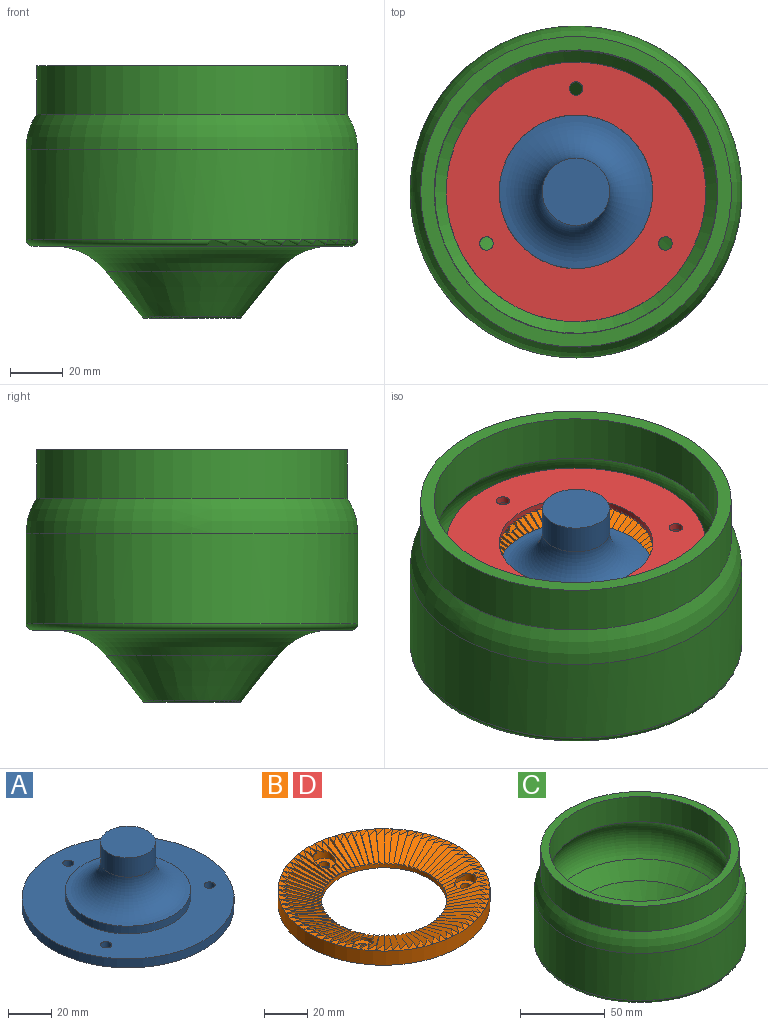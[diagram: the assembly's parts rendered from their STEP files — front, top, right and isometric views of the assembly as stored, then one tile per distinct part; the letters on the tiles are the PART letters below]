
ASSEMBLY  parts=4 mates=3
PART A: 10 faces, bbox 98x98x36.7 mm
  f0: cylinder r=12.7mm len=25.4mm, axis (0,0,1), area 874.5mm2, adj f1,f6
  f1: torus R=28.95mm, axis (0,0,1), area 2983.7mm2, adj f0,f2
  f2: cylinder r=28.95mm len=57.9mm, axis (0,0,1), area 794.3mm2, adj f1,f3
  f3: plane 98x98mm, normal (0,0,1), area 4848.7mm2, adj f2,f4,f7,f8,f9
  f4: cylinder r=49mm len=98mm, axis (0,0,1), area 1564mm2, adj f3,f5
  f5: plane 98x98mm, normal (0,0,-1), area 7481.5mm2, adj f4,f7,f8,f9
  f6: plane 25.4x25.4mm, normal (0,0,1), area 506.7mm2, adj f0
  f7: cylinder r=2.55mm len=5.11mm, axis (0,0,1), area 81.5mm2, adj f3,f5
  f8: cylinder r=2.55mm len=5.11mm, axis (0,0,1), area 81.5mm2, adj f3,f5
  f9: cylinder r=2.55mm len=5.11mm, axis (0,0,1), area 81.5mm2, adj f3,f5
PART B: 188 faces, bbox 98x98x8 mm
  f0: plane 5.82x2.75mm, normal (0.35,-0.3,0.89), area 14.5mm2, adj f18,f20,f24,f179
  f1: plane 4.04x2.48mm, normal (0.52,0.85,0), area 3.4mm2, adj f25,f74,f93,f183
  f2: plane 4.27x2.62mm, normal (0.52,0.85,0), area 5mm2, adj f3,f8,f24,f183
  f3: plane 5.84x4.62mm, normal (-0.42,-0.17,0.89), area 13.9mm2, adj f2,f5,f24,f183
  f4: plane 4.55x2.32mm, normal (0.45,0.89,0), area 3.9mm2, adj f25,f74,f75,f183
  f5: plane 4.72x2.67mm, normal (0.45,0.89,0), area 5.3mm2, adj f3,f24,f75,f183
  f6: plane 5.57x4.05mm, normal (0.59,0.81,0), area 6.3mm2, adj f25,f90,f93,f183
  f7: plane 5.47x3.97mm, normal (0.59,0.81,0), area 6.9mm2, adj f8,f24,f90,f183
  f8: plane 5.88x5.55mm, normal (-0.43,-0.14,0.89), area 15.8mm2, adj f2,f7,f24,f183
  f9: plane 5.84x4.62mm, normal (0.07,0.45,0.89), area 13.9mm2, adj f11,f16,f24,f181
  f10: plane 4.55x2.32mm, normal (0.45,-0.89,0), area 3.9mm2, adj f25,f137,f139,f181
  f11: plane 4.72x2.67mm, normal (0.45,-0.89,0), area 5.3mm2, adj f9,f24,f139,f181
  f12: plane 5.88x5.55mm, normal (0.04,0.45,0.89), area 15.8mm2, adj f14,f16,f24,f181
  f13: plane 5.57x4.05mm, normal (0.59,-0.81,0), area 6.3mm2, adj f25,f143,f144,f181
  f14: plane 5.47x3.97mm, normal (0.59,-0.81,0), area 6.9mm2, adj f12,f24,f144,f181
  f15: plane 4.04x2.48mm, normal (0.52,-0.85,0), area 3.4mm2, adj f25,f137,f143,f181
  f16: plane 4.27x2.62mm, normal (0.52,-0.85,0), area 5mm2, adj f9,f12,f24,f181
  f17: plane 5.75x1.73mm, normal (-1,0.08,0), area 4.8mm2, adj f25,f33,f150,f179
  f18: plane 5.81x2.84mm, normal (-1,0.08,0), area 5.8mm2, adj f0,f24,f150,f179
  f19: plane 4.63x1.39mm, normal (-1,0,0), area 3.2mm2, adj f25,f33,f167,f179
  f20: plane 4.92x2.54mm, normal (-1,0,0), area 4.9mm2, adj f0,f21,f24,f179
  f21: plane 5.82x2.86mm, normal (0.37,-0.27,0.89), area 14.5mm2, adj f20,f23,f24,f179
  f22: plane 5.75x1.73mm, normal (-1,-0.08,0), area 4.8mm2, adj f25,f167,f168,f179
  f23: plane 5.81x2.84mm, normal (-1,-0.08,0), area 5.8mm2, adj f21,f24,f168,f179
  f24: cylinder r=29mm len=58mm, axis (0,0,1), area 463.4mm2, adj f0,f2,f3,f5,f7,f8,f9,f11
  f25: plane 98x98mm, normal (0,0,1), area 803.3mm2, adj f1,f4,f6,f10,f13,f15,f17,f19
  f26: cylinder r=49mm len=98mm, axis (0,0,1), area 2463mm2, adj f25,f27
  f27: plane 98x98mm, normal (0,0,-1), area 4839.5mm2, adj f24,f26,f185,f186,f187
  f28: plane 19.16x5.91mm, normal (-0.97,0.23,0), area 20.5mm2, adj f24,f25,f29,f31
  f29: plane 19.18x6.85mm, normal (0.29,-0.35,0.89), area 57.5mm2, adj f24,f25,f28,f30
  f30: plane 19.46x5.91mm, normal (-0.99,0.16,0), area 20.5mm2, adj f24,f25,f29,f150
  f31: plane 18.76x8.3mm, normal (0.27,-0.37,0.89), area 57.5mm2, adj f24,f25,f28,f40
  f32: plane 18.21x7.54mm, normal (-0.38,-0.92,0), area 20.5mm2, adj f24,f25,f130,f151
  f33: plane 5.75x3.82mm, normal (0.35,-0.3,0.89), area 10.3mm2, adj f17,f19,f25,f179
  f34: plane 18.21x7.54mm, normal (0.92,0.38,0), area 20.5mm2, adj f24,f25,f86,f94
  f35: plane 19.65x5.91mm, normal (-0.08,1,0), area 20.5mm2, adj f24,f25,f57,f66
  f36: plane 14.99x12.8mm, normal (-0.65,0.76,0), area 20.5mm2, adj f24,f25,f48,f65
  f37: plane 17.56x8.95mm, normal (-0.89,0.45,0), area 20.5mm2, adj f24,f25,f41,f45
  f38: plane 18.21x7.54mm, normal (-0.92,0.38,0), area 20.5mm2, adj f24,f25,f39,f41
  f39: plane 18.22x9.69mm, normal (0.24,-0.39,0.89), area 57.5mm2, adj f24,f25,f38,f40
  f40: plane 18.74x6.09mm, normal (-0.95,0.31,0), area 20.5mm2, adj f24,f25,f31,f39
  f41: plane 17.57x11.03mm, normal (0.21,-0.4,0.89), area 57.5mm2, adj f24,f25,f37,f38
  f42: plane 15.96x13.49mm, normal (0.14,-0.43,0.89), area 57.5mm2, adj f24,f25,f43,f44
  f43: plane 15.94x11.58mm, normal (-0.81,0.59,0), area 20.5mm2, adj f24,f25,f42,f46
  f44: plane 16.8x10.3mm, normal (-0.85,0.52,0), area 20.5mm2, adj f24,f25,f42,f45
  f45: plane 16.82x12.3mm, normal (0.17,-0.42,0.89), area 57.5mm2, adj f24,f25,f37,f44
  f46: plane 15x14.6mm, normal (0.11,-0.44,0.89), area 57.5mm2, adj f24,f25,f43,f47
  f47: plane 14.99x12.8mm, normal (-0.76,0.65,0), area 20.5mm2, adj f24,f25,f46,f50
  f48: plane 16.54x12.81mm, normal (0.04,-0.45,0.89), area 57.5mm2, adj f24,f25,f36,f49
  f49: plane 13.93x13.93mm, normal (-0.71,0.71,0), area 20.5mm2, adj f24,f25,f48,f50
  f50: plane 15.62x13.95mm, normal (0.07,-0.45,0.89), area 57.5mm2, adj f24,f25,f47,f49
  f51: plane 19.54x7.93mm, normal (-0.14,-0.43,0.89), area 57.5mm2, adj f24,f25,f53,f64
  f52: plane 19.16x5.91mm, normal (-0.23,0.97,0), area 20.5mm2, adj f24,f25,f54,f56
  f53: plane 18.74x6.09mm, normal (-0.31,0.95,0), area 20.5mm2, adj f24,f25,f51,f54
  f54: plane 19.79x6.87mm, normal (-0.17,-0.42,0.89), area 57.5mm2, adj f24,f25,f52,f53
  f55: plane 19.46x5.91mm, normal (-0.16,0.99,0), area 20.5mm2, adj f24,f25,f56,f57
  f56: plane 19.92x5.93mm, normal (-0.21,-0.4,0.89), area 57.5mm2, adj f24,f25,f52,f55
  f57: plane 19.93x5.93mm, normal (-0.24,-0.39,0.89), area 57.5mm2, adj f24,f25,f35,f55
  f58: plane 19.17x8.93mm, normal (-0.11,-0.44,0.89), area 57.5mm2, adj f24,f25,f60,f64
  f59: plane 18.69x9.89mm, normal (-0.07,-0.45,0.89), area 57.5mm2, adj f24,f25,f60,f63
  f60: plane 17.56x8.95mm, normal (-0.45,0.89,0), area 20.5mm2, adj f24,f25,f58,f59
  f61: plane 18.08x10.78mm, normal (-0.04,-0.45,0.89), area 57.5mm2, adj f24,f25,f62,f63
  f62: plane 15.94x11.58mm, normal (-0.59,0.81,0), area 20.5mm2, adj f24,f25,f61,f65
  f63: plane 16.8x10.3mm, normal (-0.52,0.85,0), area 20.5mm2, adj f24,f25,f59,f61
  f64: plane 18.21x7.54mm, normal (-0.38,0.92,0), area 20.5mm2, adj f24,f25,f51,f58
  f65: plane 17.37x11.6mm, normal (0,-0.45,0.89), area 57.5mm2, adj f24,f25,f36,f62
  f66: plane 19.81x5.93mm, normal (-0.27,-0.37,0.89), area 57.5mm2, adj f24,f25,f35,f69
  f67: plane 19.16x5.91mm, normal (0.23,0.97,0), area 20.5mm2, adj f24,f25,f73,f79
  f68: plane 19.65x5.91mm, normal (0.08,1,0), area 20.5mm2, adj f24,f25,f70,f72
  f69: plane 19.71x5.91mm, normal (0,1,0), area 20.5mm2, adj f24,f25,f66,f70
  f70: plane 19.66x5.93mm, normal (-0.3,-0.35,0.89), area 57.5mm2, adj f24,f25,f68,f69
  f71: plane 19.46x5.91mm, normal (0.16,0.99,0), area 20.5mm2, adj f24,f25,f72,f73
  f72: plane 19.48x5.93mm, normal (-0.32,-0.32,0.89), area 57.5mm2, adj f24,f25,f68,f71
  f73: plane 19.18x6.85mm, normal (-0.35,-0.29,0.89), area 57.5mm2, adj f24,f25,f67,f71
  f74: plane 5.66x4.04mm, normal (-0.42,-0.17,0.89), area 9.4mm2, adj f1,f4,f25,f183
  f75: plane 17.57x11.03mm, normal (-0.4,-0.21,0.89), area 34.6mm2, adj f4,f5,f24,f25,f78,f183
  f76: plane 18.22x9.69mm, normal (-0.39,-0.24,0.89), area 57.5mm2, adj f24,f25,f77,f78
  f77: plane 18.74x6.09mm, normal (0.31,0.95,0), area 20.5mm2, adj f24,f25,f76,f79
  f78: plane 18.21x7.54mm, normal (0.38,0.92,0), area 20.5mm2, adj f24,f25,f75,f76
  f79: plane 18.76x8.3mm, normal (-0.37,-0.27,0.89), area 57.5mm2, adj f24,f25,f67,f77
  f80: plane 17.37x11.6mm, normal (-0.45,0,0.89), area 57.5mm2, adj f24,f25,f82,f92
  f81: plane 16.8x10.3mm, normal (0.85,0.52,0), area 20.5mm2, adj f24,f25,f83,f85
  f82: plane 15.94x11.58mm, normal (0.81,0.59,0), area 20.5mm2, adj f24,f25,f80,f83
  f83: plane 18.08x10.78mm, normal (-0.45,0.04,0.89), area 57.5mm2, adj f24,f25,f81,f82
  f84: plane 17.56x8.95mm, normal (0.89,0.45,0), area 20.5mm2, adj f24,f25,f85,f86
  f85: plane 18.69x9.89mm, normal (-0.45,0.07,0.89), area 57.5mm2, adj f24,f25,f81,f84
  f86: plane 19.17x8.93mm, normal (-0.44,0.11,0.89), area 57.5mm2, adj f24,f25,f34,f84
  f87: plane 16.54x12.81mm, normal (-0.45,-0.04,0.89), area 57.5mm2, adj f24,f25,f89,f92
  f88: plane 15.62x13.95mm, normal (-0.45,-0.07,0.89), area 57.5mm2, adj f24,f25,f89,f91
  f89: plane 13.93x13.93mm, normal (0.71,0.71,0), area 20.5mm2, adj f24,f25,f87,f88
  f90: plane 15x14.6mm, normal (-0.44,-0.11,0.89), area 52.8mm2, adj f6,f7,f24,f25,f91,f183
  f91: plane 14.99x12.8mm, normal (0.65,0.76,0), area 20.5mm2, adj f24,f25,f88,f90
  f92: plane 14.99x12.8mm, normal (0.76,0.65,0), area 20.5mm2, adj f24,f25,f80,f87
  f93: plane 5.66x5.57mm, normal (-0.43,-0.14,0.89), area 12.4mm2, adj f1,f6,f25,f183
  f94: plane 19.54x7.93mm, normal (-0.43,0.14,0.89), area 57.5mm2, adj f24,f25,f34,f99
  f95: plane 14.99x12.8mm, normal (0.76,-0.65,0), area 20.5mm2, adj f24,f25,f121,f149
  f96: plane 19.16x5.91mm, normal (0.97,-0.23,0), area 20.5mm2, adj f24,f25,f104,f111
  f97: plane 19.65x5.91mm, normal (1,0.08,0), area 20.5mm2, adj f24,f25,f103,f110
  f98: plane 19.16x5.91mm, normal (0.97,0.23,0), area 20.5mm2, adj f24,f25,f100,f102
  f99: plane 18.74x6.09mm, normal (0.95,0.31,0), area 20.5mm2, adj f24,f25,f94,f100
  f100: plane 19.79x6.87mm, normal (-0.42,0.17,0.89), area 57.5mm2, adj f24,f25,f98,f99
  f101: plane 19.46x5.91mm, normal (0.99,0.16,0), area 20.5mm2, adj f24,f25,f102,f103
  f102: plane 19.92x5.93mm, normal (-0.4,0.21,0.89), area 57.5mm2, adj f24,f25,f98,f101
  f103: plane 19.93x5.93mm, normal (-0.39,0.24,0.89), area 57.5mm2, adj f24,f25,f97,f101
  f104: plane 19.18x6.85mm, normal (-0.29,0.35,0.89), area 57.5mm2, adj f24,f25,f96,f106
  f105: plane 19.48x5.93mm, normal (-0.32,0.32,0.89), area 57.5mm2, adj f24,f25,f106,f109
  f106: plane 19.46x5.91mm, normal (0.99,-0.16,0), area 20.5mm2, adj f24,f25,f104,f105
  f107: plane 19.66x5.93mm, normal (-0.35,0.3,0.89), area 57.5mm2, adj f24,f25,f108,f109
  f108: plane 19.71x5.91mm, normal (1,0,0), area 20.5mm2, adj f24,f25,f107,f110
  f109: plane 19.65x5.91mm, normal (1,-0.08,0), area 20.5mm2, adj f24,f25,f105,f107
  f110: plane 19.81x5.93mm, normal (-0.37,0.27,0.89), area 57.5mm2, adj f24,f25,f97,f108
  f111: plane 18.76x8.3mm, normal (-0.27,0.37,0.89), area 57.5mm2, adj f24,f25,f96,f113
  f112: plane 18.21x7.54mm, normal (0.92,-0.38,0), area 20.5mm2, adj f24,f25,f114,f115
  f113: plane 18.74x6.09mm, normal (0.95,-0.31,0), area 20.5mm2, adj f24,f25,f111,f114
  f114: plane 18.22x9.69mm, normal (-0.24,0.39,0.89), area 57.5mm2, adj f24,f25,f112,f113
  f115: plane 17.57x11.03mm, normal (-0.21,0.4,0.89), area 57.5mm2, adj f24,f25,f112,f117
  f116: plane 16.8x10.3mm, normal (0.85,-0.52,0), area 20.5mm2, adj f24,f25,f118,f120
  f117: plane 17.56x8.95mm, normal (0.89,-0.45,0), area 20.5mm2, adj f24,f25,f115,f118
  f118: plane 16.82x12.3mm, normal (-0.17,0.42,0.89), area 57.5mm2, adj f24,f25,f116,f117
  f119: plane 15.94x11.58mm, normal (0.81,-0.59,0), area 20.5mm2, adj f24,f25,f120,f121
  f120: plane 15.96x13.49mm, normal (-0.14,0.43,0.89), area 57.5mm2, adj f24,f25,f116,f119
  f121: plane 15x14.6mm, normal (-0.11,0.44,0.89), area 57.5mm2, adj f24,f25,f95,f119
  f122: plane 19.92x5.93mm, normal (0.21,0.4,0.89), area 57.5mm2, adj f24,f25,f125,f148
  f123: plane 19.65x5.91mm, normal (-0.08,-1,0), area 20.5mm2, adj f24,f25,f129,f136
  f124: plane 19.65x5.91mm, normal (0.08,-1,0), area 20.5mm2, adj f24,f25,f126,f128
  f125: plane 19.46x5.91mm, normal (0.16,-0.99,0), area 20.5mm2, adj f24,f25,f122,f126
  f126: plane 19.93x5.93mm, normal (0.24,0.39,0.89), area 57.5mm2, adj f24,f25,f124,f125
  f127: plane 19.71x5.91mm, normal (0,-1,0), area 20.5mm2, adj f24,f25,f128,f129
  f128: plane 19.81x5.93mm, normal (0.27,0.37,0.89), area 57.5mm2, adj f24,f25,f124,f127
  f129: plane 19.66x5.93mm, normal (0.3,0.35,0.89), area 57.5mm2, adj f24,f25,f123,f127
  f130: plane 18.22x9.69mm, normal (0.39,0.24,0.89), area 57.5mm2, adj f24,f25,f32,f132
  f131: plane 18.76x8.3mm, normal (0.37,0.27,0.89), area 57.5mm2, adj f24,f25,f132,f135
  f132: plane 18.74x6.09mm, normal (-0.31,-0.95,0), area 20.5mm2, adj f24,f25,f130,f131
  f133: plane 19.18x6.85mm, normal (0.35,0.29,0.89), area 57.5mm2, adj f24,f25,f134,f135
  f134: plane 19.46x5.91mm, normal (-0.16,-0.99,0), area 20.5mm2, adj f24,f25,f133,f136
  f135: plane 19.16x5.91mm, normal (-0.23,-0.97,0), area 20.5mm2, adj f24,f25,f131,f133
  f136: plane 19.48x5.93mm, normal (0.32,0.32,0.89), area 57.5mm2, adj f24,f25,f123,f134
  f137: plane 5.91x3.24mm, normal (0.07,0.45,0.89), area 9.4mm2, adj f10,f15,f25,f181
  f138: plane 18.21x7.54mm, normal (0.38,-0.92,0), area 20.5mm2, adj f24,f25,f139,f141
  f139: plane 19.17x8.93mm, normal (0.11,0.44,0.89), area 34.6mm2, adj f10,f11,f24,f25,f138,f181
  f140: plane 18.74x6.09mm, normal (0.31,-0.95,0), area 20.5mm2, adj f24,f25,f141,f142
  f141: plane 19.54x7.93mm, normal (0.14,0.43,0.89), area 57.5mm2, adj f24,f25,f138,f140
  f142: plane 19.79x6.87mm, normal (0.17,0.42,0.89), area 57.5mm2, adj f24,f25,f140,f148
  f143: plane 7.7x2.95mm, normal (0.04,0.45,0.89), area 12.4mm2, adj f13,f15,f25,f181
  f144: plane 17.37x11.6mm, normal (0,0.45,0.89), area 52.8mm2, adj f13,f14,f24,f25,f147,f181
  f145: plane 16.54x12.81mm, normal (-0.04,0.45,0.89), area 57.5mm2, adj f24,f25,f146,f147
  f146: plane 13.93x13.93mm, normal (0.71,-0.71,0), area 20.5mm2, adj f24,f25,f145,f149
  f147: plane 14.99x12.8mm, normal (0.65,-0.76,0), area 20.5mm2, adj f24,f25,f144,f145
  f148: plane 19.16x5.91mm, normal (0.23,-0.97,0), area 20.5mm2, adj f24,f25,f122,f142
  f149: plane 15.62x13.95mm, normal (-0.07,0.45,0.89), area 57.5mm2, adj f24,f25,f95,f146
  f150: plane 19.48x5.93mm, normal (0.32,-0.32,0.89), area 44.6mm2, adj f17,f18,f24,f25,f30,f179
  f151: plane 17.57x11.03mm, normal (0.4,0.21,0.89), area 57.5mm2, adj f24,f25,f32,f155
  f152: plane 16.8x10.3mm, normal (-0.85,-0.52,0), area 20.5mm2, adj f24,f25,f160,f178
  f153: plane 14.99x12.8mm, normal (-0.65,-0.76,0), area 20.5mm2, adj f24,f25,f159,f166
  f154: plane 16.8x10.3mm, normal (-0.52,-0.85,0), area 20.5mm2, adj f24,f25,f156,f158
  f155: plane 17.56x8.95mm, normal (-0.45,-0.89,0), area 20.5mm2, adj f24,f25,f151,f156
  f156: plane 16.82x12.3mm, normal (0.42,0.17,0.89), area 57.5mm2, adj f24,f25,f154,f155
  f157: plane 15.94x11.58mm, normal (-0.59,-0.81,0), area 20.5mm2, adj f24,f25,f158,f159
  f158: plane 15.96x13.49mm, normal (0.43,0.14,0.89), area 57.5mm2, adj f24,f25,f154,f157
  f159: plane 15x14.6mm, normal (0.44,0.11,0.89), area 57.5mm2, adj f24,f25,f153,f157
  f160: plane 18.08x10.78mm, normal (0.45,-0.04,0.89), area 57.5mm2, adj f24,f25,f152,f162
  f161: plane 17.37x11.6mm, normal (0.45,0,0.89), area 57.5mm2, adj f24,f25,f162,f165
  f162: plane 15.94x11.58mm, normal (-0.81,-0.59,0), area 20.5mm2, adj f24,f25,f160,f161
  f163: plane 16.54x12.81mm, normal (0.45,0.04,0.89), area 57.5mm2, adj f24,f25,f164,f165
  f164: plane 13.93x13.93mm, normal (-0.71,-0.71,0), area 20.5mm2, adj f24,f25,f163,f166
  f165: plane 14.99x12.8mm, normal (-0.76,-0.65,0), area 20.5mm2, adj f24,f25,f161,f163
  f166: plane 15.62x13.95mm, normal (0.45,0.07,0.89), area 57.5mm2, adj f24,f25,f153,f164
  f167: plane 5.9x3.46mm, normal (0.37,-0.27,0.89), area 10.3mm2, adj f19,f22,f25,f179
  f168: plane 19.93x5.93mm, normal (0.39,-0.24,0.89), area 44.6mm2, adj f22,f23,f24,f25,f170,f179
  f169: plane 19.92x5.93mm, normal (0.4,-0.21,0.89), area 57.5mm2, adj f24,f25,f170,f177
  f170: plane 19.46x5.91mm, normal (-0.99,-0.16,0), area 20.5mm2, adj f24,f25,f168,f169
  f171: plane 19.79x6.87mm, normal (0.42,-0.17,0.89), area 57.5mm2, adj f24,f25,f173,f177
  f172: plane 19.54x7.93mm, normal (0.43,-0.14,0.89), area 57.5mm2, adj f24,f25,f173,f176
  f173: plane 18.74x6.09mm, normal (-0.95,-0.31,0), area 20.5mm2, adj f24,f25,f171,f172
  f174: plane 19.17x8.93mm, normal (0.44,-0.11,0.89), area 57.5mm2, adj f24,f25,f175,f176
  f175: plane 17.56x8.95mm, normal (-0.89,-0.45,0), area 20.5mm2, adj f24,f25,f174,f178
  f176: plane 18.21x7.54mm, normal (-0.92,-0.38,0), area 20.5mm2, adj f24,f25,f172,f174
  f177: plane 19.16x5.91mm, normal (-0.97,-0.23,0), area 20.5mm2, adj f24,f25,f169,f171
  f178: plane 18.69x9.89mm, normal (0.45,-0.07,0.89), area 57.5mm2, adj f24,f25,f152,f175
  f179: cylinder r=5.08mm len=10.16mm, axis (0,0,-1), area 96.7mm2, adj f0,f17,f18,f19,f20,f21,f22,f23
  f180: plane 10.16x10.16mm, normal (0,0,1), area 60.6mm2, adj f179,f186
  f181: cylinder r=5.08mm len=10.16mm, axis (0,0,-1), area 92.6mm2, adj f9,f10,f11,f12,f13,f14,f15,f16
  f182: plane 10.16x10.16mm, normal (0,0,1), area 60.6mm2, adj f181,f185
  f183: cylinder r=5.08mm len=10.16mm, axis (0,0,-1), area 100.7mm2, adj f1,f2,f3,f4,f5,f6,f7,f8
  f184: plane 10.16x10.16mm, normal (0,0,1), area 60.6mm2, adj f183,f187
  f185: cylinder r=2.55mm len=5.11mm, axis (0,0,1), area 43.8mm2, adj f27,f182
  f186: cylinder r=2.55mm len=5.11mm, axis (0,0,1), area 43.8mm2, adj f27,f180
  f187: cylinder r=2.55mm len=5.11mm, axis (0,0,1), area 43.8mm2, adj f27,f184
PART C: 23 faces, bbox 135.6x135.6x95.2 mm
  f0: cylinder r=58.63mm len=117.26mm, axis (0,0,-1), area 6747.5mm2, adj f1,f11
  f1: torus R=39.05mm, axis (0,0,-1), area 5376.3mm2, adj f0,f2
  f2: cylinder r=62.64mm len=125.29mm, axis (0,0,-1), area 13382mm2, adj f1,f21
  f3: plane 120.21x120.21mm, normal (0,0,-1), area 2617.6mm2, adj f13,f15,f17,f19,f20,f21
  f4: cone r=18.05mm half-angle=38.5deg, axis (0,0,1), area 3527.9mm2, adj f20,f22
  f5: cone r=16.06mm half-angle=51.5deg, axis (0,0,-1), area 132.1mm2, adj f6,f22
  f6: torus R=17.64mm, axis (0,0,-1), area 385.3mm2, adj f5,f7
  f7: cone r=44.37mm half-angle=38.5deg, axis (0,0,1), area 8704.1mm2, adj f6,f8
  f8: cone r=44.37mm half-angle=43.3deg, axis (0,0,1), area 4013.7mm2, adj f7,f9
  f9: torus R=39.05mm, axis (0,0,-1), area 10503mm2, adj f8,f10
  f10: cylinder r=53.55mm len=107.1mm, axis (0,0,-1), area 6135.6mm2, adj f9,f11
  f11: plane 117.26x117.26mm, normal (0,0,1), area 1790.3mm2, adj f0,f10
  f12: cone r=0mm half-angle=59deg, axis (0,0,-1), area 35.8mm2, adj f13
  f13: cylinder r=3.12mm len=12.7mm, axis (0,0,-1), area 249.3mm2, adj f3,f12
  f14: cone r=0mm half-angle=59deg, axis (0,0,-1), area 35.8mm2, adj f15
  f15: cylinder r=3.12mm len=12.7mm, axis (0,0,-1), area 249.3mm2, adj f3,f14
  f16: cone r=0mm half-angle=59deg, axis (0,0,-1), area 35.8mm2, adj f17
  f17: cylinder r=3.12mm len=12.7mm, axis (0,0,-1), area 249.3mm2, adj f3,f16
  f18: cone r=0mm half-angle=59deg, axis (0,0,-1), area 35.8mm2, adj f19
  f19: cylinder r=3.12mm len=12.7mm, axis (0,0,-1), area 249.3mm2, adj f3,f18
  f20: torus R=52.35mm, axis (0,0,1), area 5981.3mm2, adj f3,f4
  f21: torus R=60.1mm, axis (0,0,1), area 1547.2mm2, adj f2,f3
  f22: torus R=17.85mm, axis (0,0,1), area 225.3mm2, adj f4,f5
PART D: same geometry as B
PLACE A t=(0,0,4.37)mm
PLACE B t=(0,0,4)mm
PLACE C t=(0,0,-9.65)mm
PLACE D rot(axis=(0,1,0),180deg) t=(0,0,11.75)mm
MATE fastened A.f1 <-> B.f26  axis (0,0,1) through (0,0,0)mm
MATE fastened B.f26 <-> D.f26  axis (0,0,1) through (0,0,8)mm
MATE fastened C.f0 <-> D.f26  axis (0,0,-1) through (0,0,-9.65)mm
